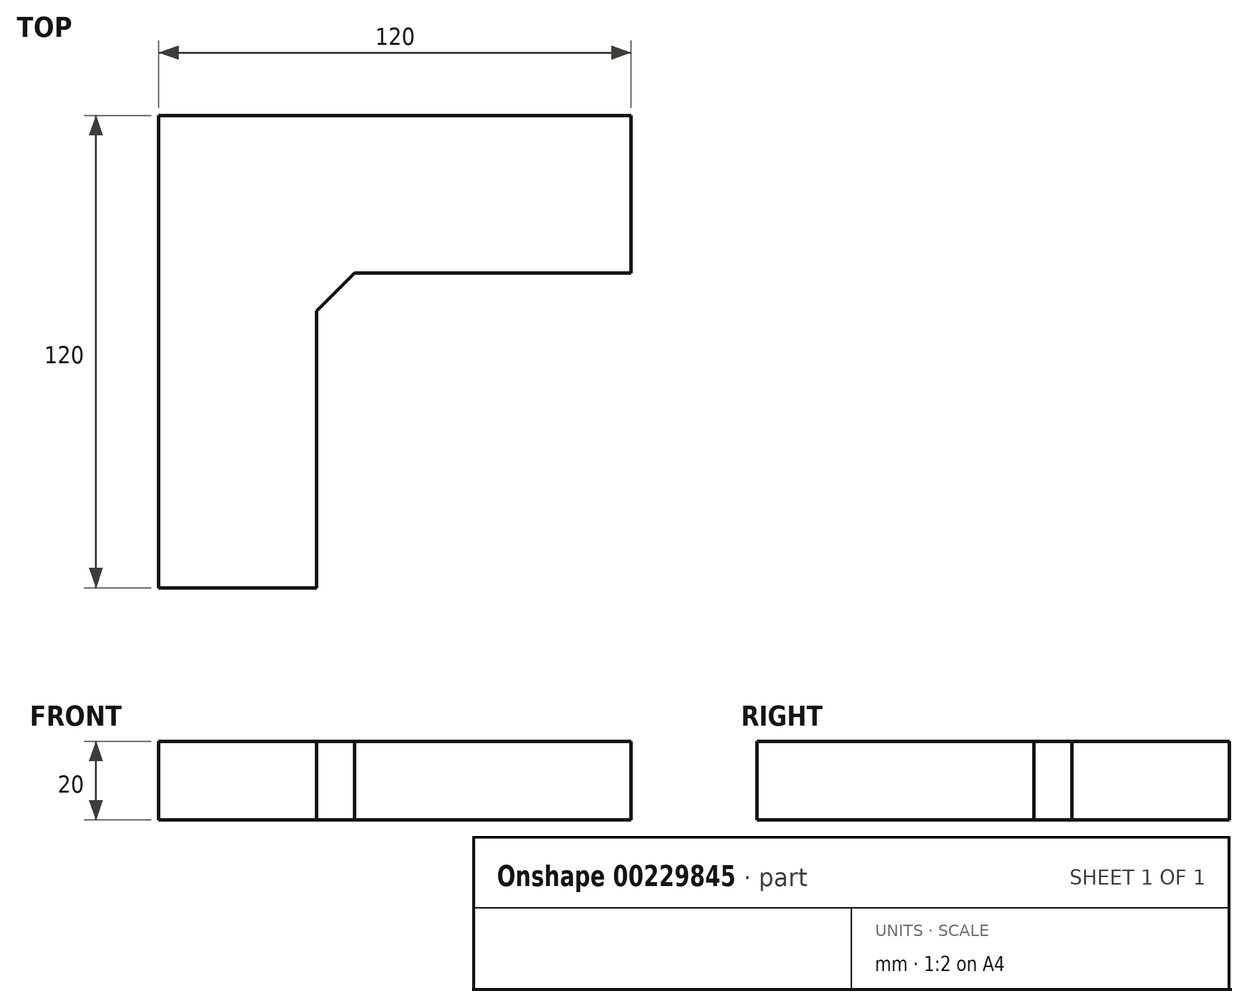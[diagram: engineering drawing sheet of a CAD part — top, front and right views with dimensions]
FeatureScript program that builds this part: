
annotation { "Feature Type Name" : "Feature", "Feature Type Description" : "" }
export const myFeature = defineFeature(function(context is Context, id is Id, definition is map)
    precondition{}
    {
        {
            var Q0;
            Q0=qCreatedBy(makeId("Top.planeOp"),FACE);
            var sketch = newSketch(context, id + "F0", { "sketchPlane" : qUnion([Q0])});
            skLineSegment(sketch, "E0.bottom", {"start": v(0, 0) * mm, "end": v(120, 0) * mm});
            skLineSegment(sketch, "E0.top", {"start": v(0, -120) * mm, "end": v(40, -120) * mm});
            skLineSegment(sketch, "E0.left", {"start": v(0, 0) * mm, "end": v(0, -120) * mm});
            skLineSegment(sketch, "E0.right", {"start": v(120, 0) * mm, "end": v(120, -40) * mm});
            skLineSegment(sketch, "E1.top", {"start": v(120, -40) * mm, "end": v(49.7, -40) * mm});
            skLineSegment(sketch, "E1.right", {"start": v(40, -120) * mm, "end": v(40, -49.7) * mm});
            skLineSegment(sketch, "E2", {"start": v(40, -49.7) * mm, "end": v(49.7, -40) * mm});
            skSolve(sketch);
        }
        {
            var Q0;
            Q0=makeQuery(id+"F0.imprint","IMPRINT",FACE,{"disambiguationData":[TD([[makeQuery(id+"F0.imprint","IMPRINT",EDGE,{"derivedFrom":sQuery(id+"F0.wireOp",EDGE,"E0.bottom")}),-1.0]])]});
            extrude(context, id + "F1", {"entities" : qUnion([Q0]), "depth" : 20 * mm});
        }
    });
